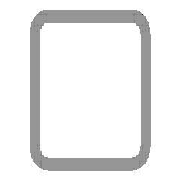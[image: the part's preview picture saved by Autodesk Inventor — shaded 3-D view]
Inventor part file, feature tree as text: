
AUTODESK INVENTOR PART (.ipt)
format: ipt  version: 2021 (Build 250183000, 183)  size: 130,560 bytes
history: native  units: mm (DEFAULTED — no unit token found)
features: other x4, sketch x3, extrude x1, plane x1
ambient origin geometry x8: Origin, YZ Plane, XZ Plane, XY Plane, X Axis, Y Axis, Z Axis, Center Point
bodies: Solid1 (feature_tree)
feature tree (9):
  parser-record x1  (decoder bookkeeping rows leaked as tree rows — omitted from the tree; the rows remain in map.json)
  other  "Driven Length"
  other  "Plano inicial"
  other  "Plano final"
  extrude  "Corpo"  TaperAngle=0.0deg  [1 undecoded]
  sketch  "Esboço"  dims[d11=50.8mm d12=4.7625mm d13=-0.0mm d14=1414.213562mm d15=25.4mm d16=25.4mm d17=9.525mm d18=90.0deg d19=1414.213562mm]
  sketch  "Sketch3"  dims[d3=1414.213562mm d4=0.0mm]
  plane  "Work Plane3"
  sketch  "Sketch4"  dims[d10=50.8mm]
note: 1 required parameter value undecoded (feature->parameter linkage not recoverable at this tier; creation-order binding heuristic only, values carry confidence <= 0.55)
